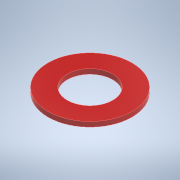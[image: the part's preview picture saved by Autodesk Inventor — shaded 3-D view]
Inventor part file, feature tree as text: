
AUTODESK INVENTOR PART (.ipt)
format: ipt  version: 2021 (Build 250183000, 183)  size: 99,840 bytes
history: native  units: mm
features: extrude x1, sketch x1
ambient origin geometry x8: Origin, YZ Plane, XZ Plane, XY Plane, X Axis, Y Axis, Z Axis, Center Point
bodies: Solid1 (feature_tree)
feature tree (2):
  extrude  "Extrusion1"  Depth=1.4mm
  sketch  "Sketch1"  dims[d0=13.0mm d1=24.0mm d2=1.4mm d3=0.0mm]
